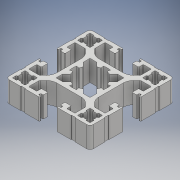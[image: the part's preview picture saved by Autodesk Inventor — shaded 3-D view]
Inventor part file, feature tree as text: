
AUTODESK INVENTOR PART (.ipt)
format: ipt  version: 2018 (Build 220112000, 112)  size: 589,824 bytes
history: native  units: mm
features: other x1, extrude x1, sketch x1
ambient origin geometry x8: Origin, YZ Plane, XZ Plane, XY Plane, X Axis, Y Axis, Z Axis, Center Point
bodies: Body1 (feature_tree)
feature tree (3):
  other  "Sólido1"
  extrude  "Extrusão1"  [1 undecoded]
  sketch  "Esboço1"  dims[d0=10.0mm d1=0.0mm]
note: 1 required parameter value undecoded (feature->parameter linkage not recoverable at this tier; creation-order binding heuristic only, values carry confidence <= 0.55)
